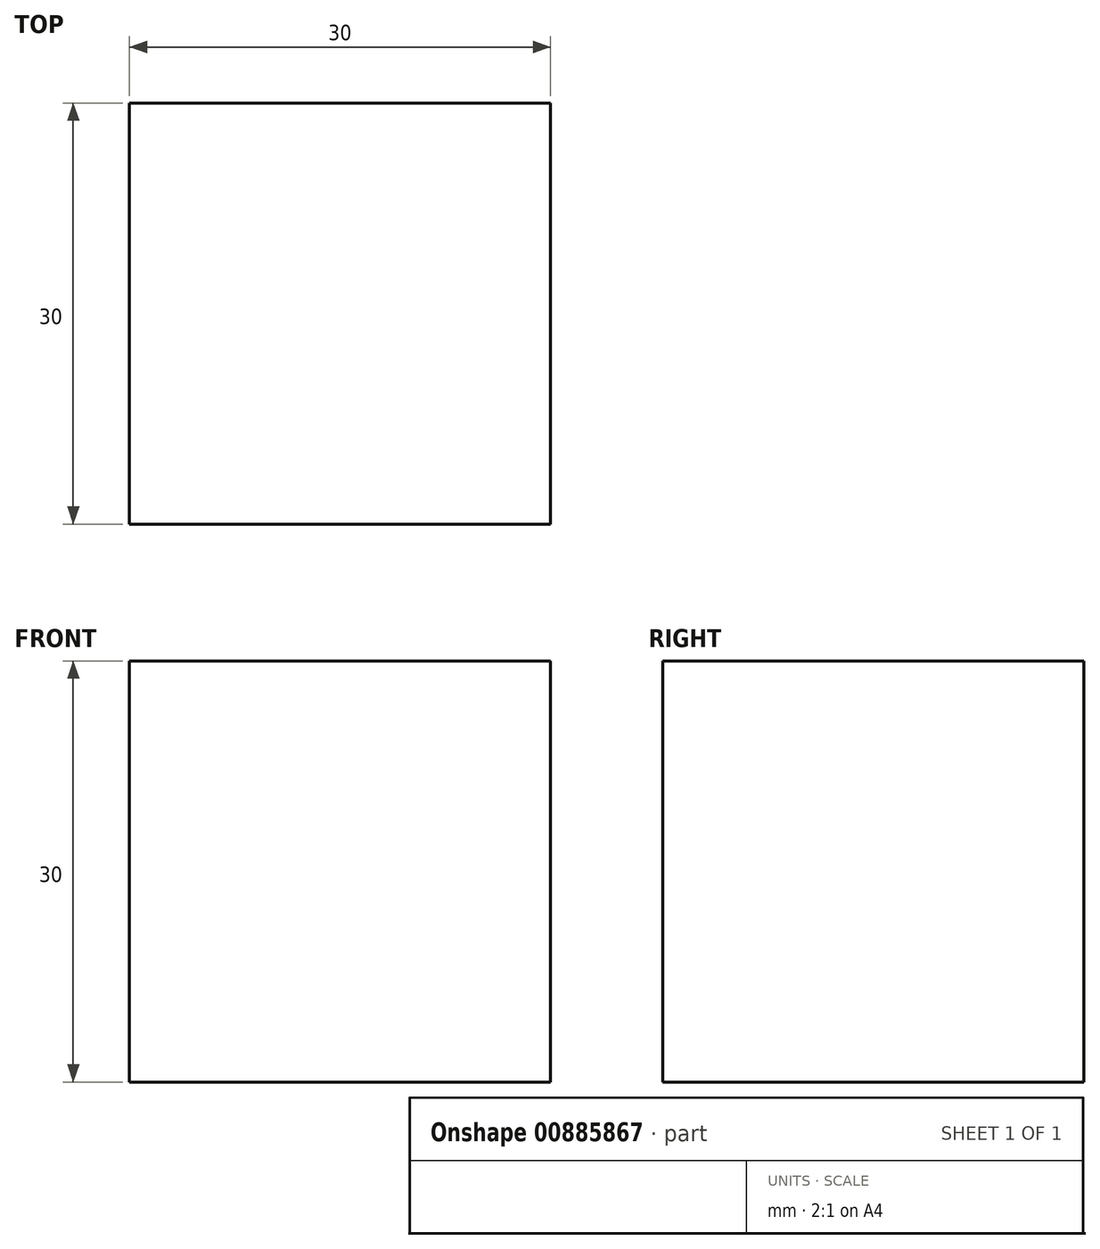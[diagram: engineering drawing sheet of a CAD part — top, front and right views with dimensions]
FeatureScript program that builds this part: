
annotation { "Feature Type Name" : "Feature", "Feature Type Description" : "" }
export const myFeature = defineFeature(function(context is Context, id is Id, definition is map)
    precondition{}
    {
        {
            var Q0;
            Q0=qCreatedBy(makeId("Top.planeOp"),FACE);
            var sketch = newSketch(context, id + "F0", { "sketchPlane" : qUnion([Q0])});
            skLineSegment(sketch, "E0.bottom", {"start": v(15, 15) * mm, "end": v(-15, 15) * mm});
            skLineSegment(sketch, "E0.top", {"start": v(15, -15) * mm, "end": v(-15, -15) * mm});
            skLineSegment(sketch, "E0.left", {"start": v(15, 15) * mm, "end": v(15, -15) * mm});
            skLineSegment(sketch, "E0.right", {"start": v(-15, 15) * mm, "end": v(-15, -15) * mm});
            skPoint(sketch, "E0.middle", {"position": v(0, 0) * mm});
            skSolve(sketch);
        }
        {
            var Q0;
            Q0=makeQuery(id+"F0.imprint","IMPRINT",FACE,{"disambiguationData":[TD([[makeQuery(id+"F0.imprint","IMPRINT",EDGE,{"derivedFrom":sQuery(id+"F0.wireOp",EDGE,"E0.bottom")}),1.0]])]});
            extrude(context, id + "F1", {"entities" : qUnion([Q0]), "depth" : 30 * mm, "offsetDistance" : 25 * mm});
        }
    });
